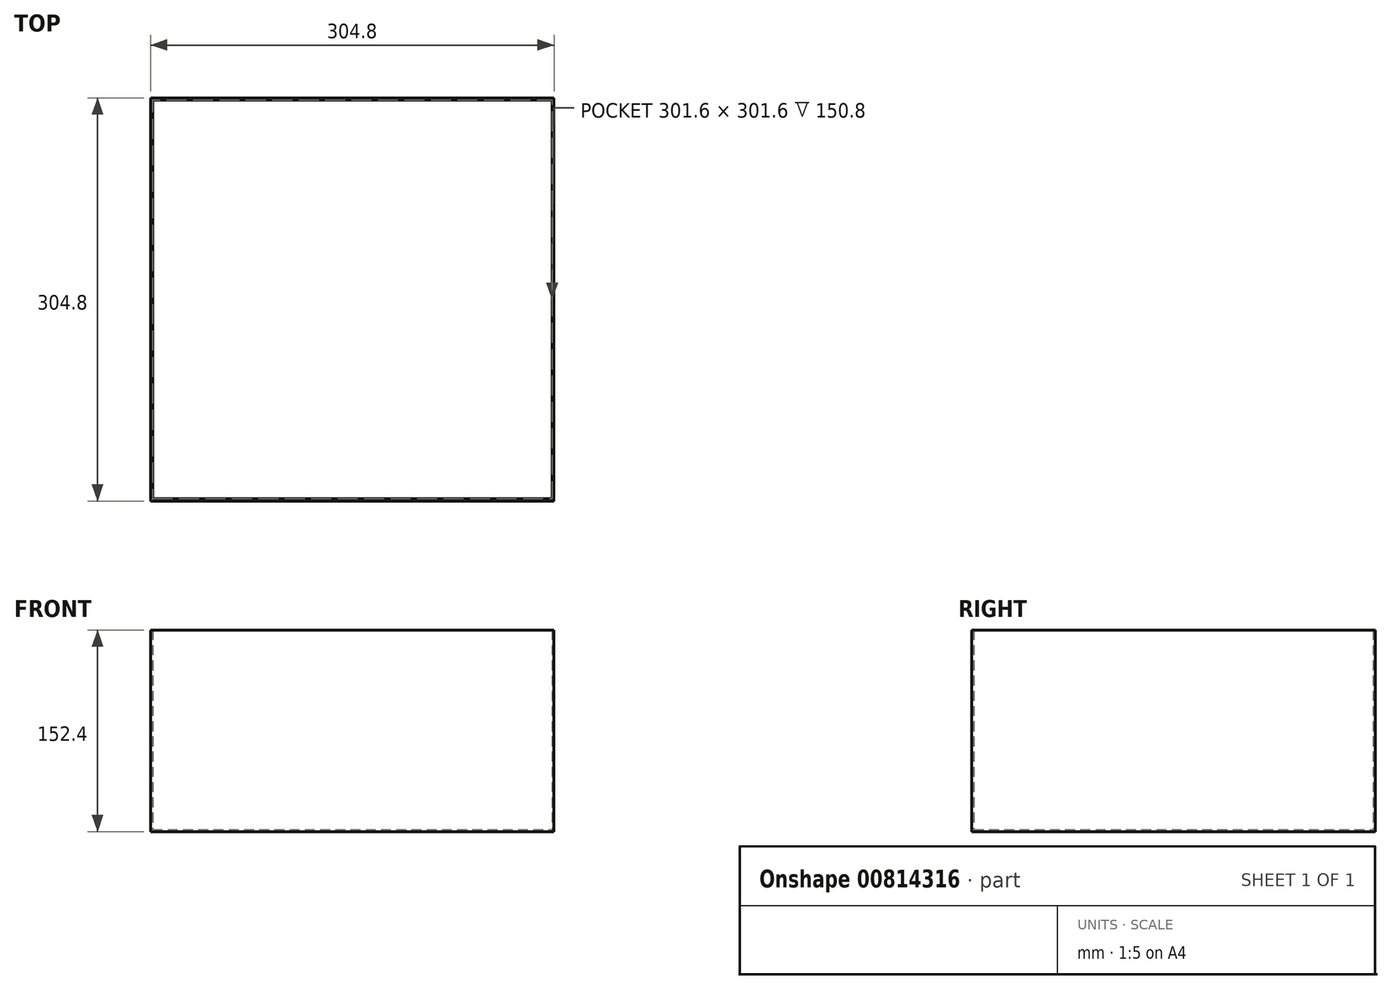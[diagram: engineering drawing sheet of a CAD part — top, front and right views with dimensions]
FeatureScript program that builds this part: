
annotation { "Feature Type Name" : "Feature", "Feature Type Description" : "" }
export const myFeature = defineFeature(function(context is Context, id is Id, definition is map)
    precondition{}
    {
        {
            var Q0;
            Q0=qCreatedBy(makeId("Top.planeOp"),FACE);
            var sketch = newSketch(context, id + "F0", { "sketchPlane" : qUnion([Q0])});
            skLineSegment(sketch, "E0", {"start": v(-184.58, 0) * mm, "end": v(120.22, 0) * mm});
            skLineSegment(sketch, "E1.0", {"start": v(-184.58, 304.8) * mm, "end": v(120.22, 304.8) * mm});
            skLineSegment(sketch, "E2", {"start": v(120.22, 0) * mm, "end": v(120.22, 304.8) * mm});
            skLineSegment(sketch, "E3.0", {"start": v(-184.58, 0) * mm, "end": v(-184.58, 304.8) * mm});
            skPoint(sketch, "E4.orphan", {"position": v(-118.3, 0) * mm});
            skSolve(sketch);
        }
        {
            var Q0;
            Q0 = qSketchRegion(id + "F0", true);
            extrude(context, id + "F1", {"entities" : qUnion([Q0]), "depth" : 152.4 * mm, "offsetDistance" : 25.4 * mm});
        }
        {
            var Q0;
            Q0=makeQuery(id+"F1.opExtrude","CAP_FACE",FACE,{"disambiguationData":[OSD([sQuery(id+"F0.wireOp",EDGE,"E0"),sQuery(id+"F0.wireOp",EDGE,"E1.0"),sQuery(id+"F0.wireOp",EDGE,"E2"),sQuery(id+"F0.wireOp",EDGE,"E3.0")])],"isStart":false});
            shell(context, id + "F2", {"entities" : qUnion([Q0]), "thickness" : 1.6 * mm});
        }
    });
